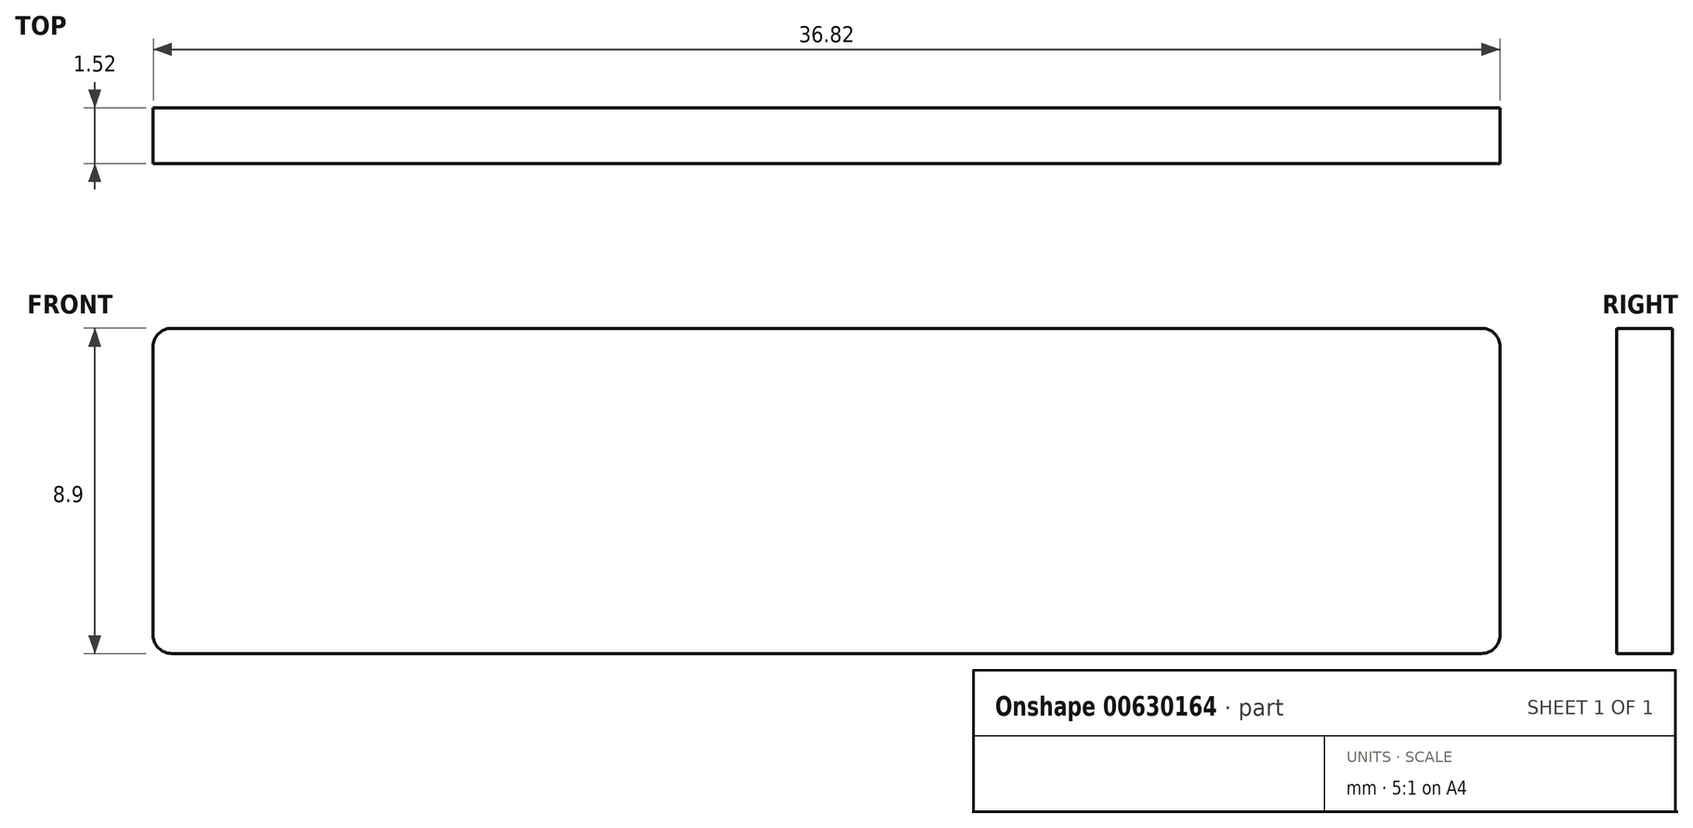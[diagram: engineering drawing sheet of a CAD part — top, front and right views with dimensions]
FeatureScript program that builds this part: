
annotation { "Feature Type Name" : "Feature", "Feature Type Description" : "" }
export const myFeature = defineFeature(function(context is Context, id is Id, definition is map)
    precondition{}
    {
        {
            var Q0;
            Q0=qCreatedBy(makeId("Front.planeOp"),FACE);
            var sketch = newSketch(context, id + "F0", { "sketchPlane" : qUnion([Q0])});
            skLineSegment(sketch, "E0.bottom", {"start": v(17.9, -4.44) * mm, "end": v(-17.9, -4.45) * mm});
            skLineSegment(sketch, "E0.top", {"start": v(17.9, 4.45) * mm, "end": v(-17.9, 4.44) * mm});
            skLineSegment(sketch, "E0.left", {"start": v(18.41, -3.94) * mm, "end": v(18.41, 3.94) * mm});
            skLineSegment(sketch, "E0.right", {"start": v(-18.41, -3.94) * mm, "end": v(-18.41, 3.94) * mm});
            skPoint(sketch, "E0.middle", {"position": v(0, 0) * mm});
            skPoint(sketch, "E1.visualSharp", {"position": v(-18.41, 4.44) * mm});
            skArc(sketch, "E1.filletArc", {"start": v(-17.9, 4.44) * mm, "mid": v(-18.27, 4.3) * mm, "end": v(-18.41, 3.94) * mm});
            skPoint(sketch, "E2.visualSharp", {"position": v(-18.41, -4.45) * mm});
            skArc(sketch, "E2.filletArc", {"start": v(-18.41, -3.94) * mm, "mid": v(-18.27, -4.3) * mm, "end": v(-17.9, -4.45) * mm});
            skPoint(sketch, "E3.visualSharp", {"position": v(18.41, -4.44) * mm});
            skArc(sketch, "E3.filletArc", {"start": v(17.9, -4.44) * mm, "mid": v(18.27, -4.3) * mm, "end": v(18.41, -3.94) * mm});
            skPoint(sketch, "E4.visualSharp", {"position": v(18.41, 4.45) * mm});
            skArc(sketch, "E4.filletArc", {"start": v(18.41, 3.94) * mm, "mid": v(18.27, 4.3) * mm, "end": v(17.9, 4.45) * mm});
            skSolve(sketch);
        }
        {
            var Q0;
            Q0 = qSketchRegion(id + "F0", true);
            extrude(context, id + "F1", {"entities" : qUnion([Q0]), "depth" : 1.52 * mm, "offsetDistance" : 25.4 * mm});
        }
    });
